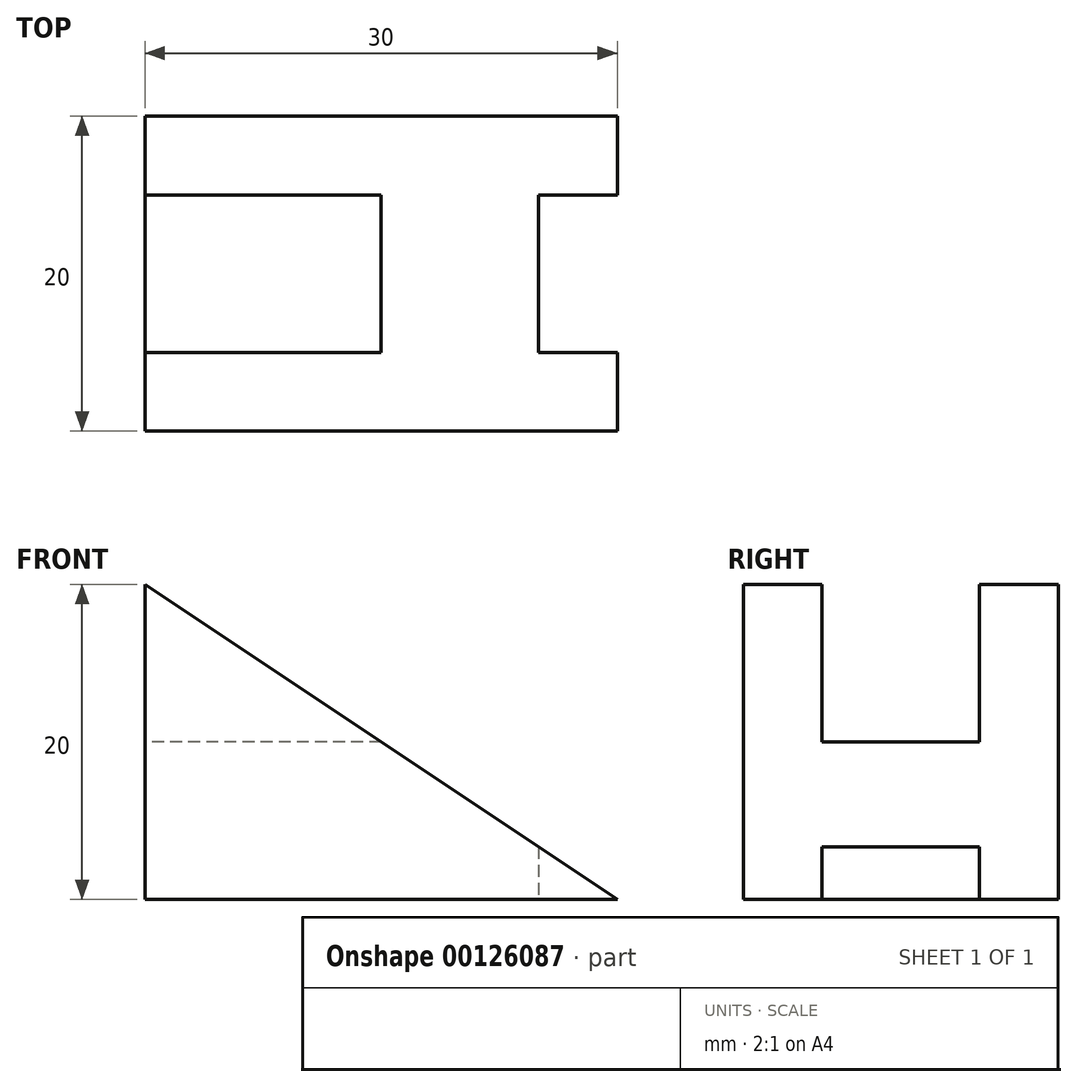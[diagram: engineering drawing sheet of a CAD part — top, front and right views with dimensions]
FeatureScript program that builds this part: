
annotation { "Feature Type Name" : "Feature", "Feature Type Description" : "" }
export const myFeature = defineFeature(function(context is Context, id is Id, definition is map)
    precondition{}
    {
        {
            var Q0;
            Q0=qCreatedBy(makeId("Front.planeOp"),FACE);
            var sketch = newSketch(context, id + "F0", { "sketchPlane" : qUnion([Q0])});
            skLineSegment(sketch, "E0", {"start": v(-30, 20) * mm, "end": v(-30, 0) * mm});
            skLineSegment(sketch, "E1", {"start": v(-30, 0) * mm, "end": v(0, 0) * mm});
            skLineSegment(sketch, "E2", {"start": v(0, 0) * mm, "end": v(-30, 20) * mm});
            skSolve(sketch);
        }
        {
            var Q0;
            Q0=makeQuery(id+"F0.imprint","IMPRINT",FACE,{"disambiguationData":[TD([[makeQuery(id+"F0.imprint","IMPRINT",EDGE,{"derivedFrom":sQuery(id+"F0.wireOp",EDGE,"E0")}),1.0]])]});
            extrude(context, id + "F1", {"entities" : qUnion([Q0]), "oppositeDirection" : true, "depth" : 20 * mm});
        }
        {
            var Q0;
            Q0=makeQuery(id+"F1.opExtrude","SWEPT_FACE",FACE,{"disambiguationData":[OSD([sQuery(id+"F0.wireOp",EDGE,"E0")])]});
            var sketch = newSketch(context, id + "F2", { "sketchPlane" : qUnion([Q0])});
            skLineSegment(sketch, "E3.bottom", {"start": v(-15, 20) * mm, "end": v(-5, 20) * mm});
            skLineSegment(sketch, "E3.top", {"start": v(-15, 10) * mm, "end": v(-5, 10) * mm});
            skLineSegment(sketch, "E3.left", {"start": v(-15, 20) * mm, "end": v(-15, 10) * mm});
            skLineSegment(sketch, "E3.right", {"start": v(-5, 20) * mm, "end": v(-5, 10) * mm});
            skSolve(sketch);
        }
        {
            var Q0;
            Q0 = qSketchRegion(id + "F2", true);
            extrude(context, id + "F3", {"entities" : qUnion([Q0]), "operationType" : NewBodyOperationType.REMOVE, "endBound" : BoundingType.THROUGH_ALL, "oppositeDirection" : true, "depth" : 25 * mm});
        }
        {
            var Q0;
            Q0=qCreatedBy(makeId("Top.planeOp"),FACE);
            var sketch = newSketch(context, id + "F4", { "sketchPlane" : qUnion([Q0])});
            skLineSegment(sketch, "E4.bottom", {"start": v(0, 15) * mm, "end": v(-5, 15) * mm});
            skLineSegment(sketch, "E4.top", {"start": v(0, 5) * mm, "end": v(-5, 5) * mm});
            skLineSegment(sketch, "E4.left", {"start": v(0, 15) * mm, "end": v(0, 5) * mm});
            skLineSegment(sketch, "E4.right", {"start": v(-5, 15) * mm, "end": v(-5, 5) * mm});
            skSolve(sketch);
        }
        {
            var Q0;
            Q0 = qSketchRegion(id + "F4", true);
            extrude(context, id + "F5", {"entities" : qUnion([Q0]), "operationType" : NewBodyOperationType.REMOVE, "depth" : 25 * mm});
        }
    });
